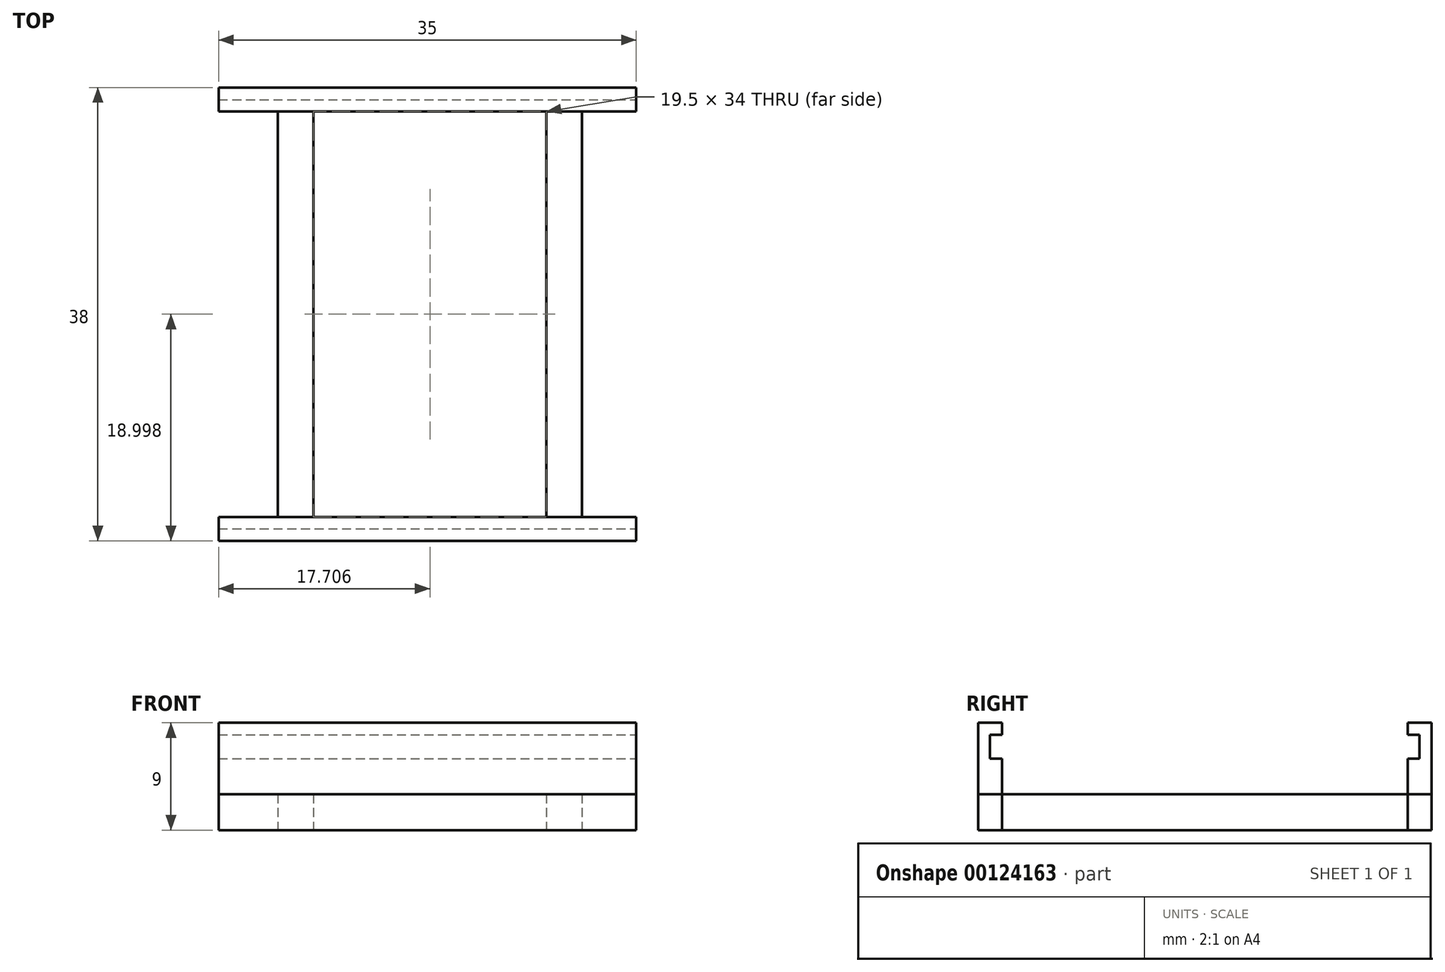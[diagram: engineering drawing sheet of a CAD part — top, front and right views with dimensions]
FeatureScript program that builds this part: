
annotation { "Feature Type Name" : "Feature", "Feature Type Description" : "" }
export const myFeature = defineFeature(function(context is Context, id is Id, definition is map)
    precondition{}
    {
        {
            var Q0;
            Q0=qCreatedBy(makeId("Top.planeOp"),FACE);
            var sketch = newSketch(context, id + "F0", { "sketchPlane" : qUnion([Q0])});
            skLineSegment(sketch, "E0.bottom", {"start": v(-16.7, 26) * mm, "end": v(18.3, 26) * mm});
            skLineSegment(sketch, "E0.top", {"start": v(-16.7, 24) * mm, "end": v(18.3, 24) * mm});
            skLineSegment(sketch, "E0.left", {"start": v(-16.7, 26) * mm, "end": v(-16.7, 24) * mm});
            skLineSegment(sketch, "E0.right", {"start": v(18.3, 26) * mm, "end": v(18.3, 24) * mm});
            skLineSegment(sketch, "E1.bottom", {"start": v(-16.7, -10) * mm, "end": v(18.3, -10) * mm});
            skLineSegment(sketch, "E1.top", {"start": v(-16.7, -12) * mm, "end": v(18.3, -12) * mm});
            skLineSegment(sketch, "E1.left", {"start": v(-16.7, -10) * mm, "end": v(-16.7, -12) * mm});
            skLineSegment(sketch, "E1.right", {"start": v(18.3, -10) * mm, "end": v(18.3, -12) * mm});
            skLineSegment(sketch, "E2.bottom", {"start": v(-11.74, 24) * mm, "end": v(-8.74, 24) * mm});
            skLineSegment(sketch, "E2.top", {"start": v(-11.74, -10) * mm, "end": v(-8.74, -10) * mm});
            skLineSegment(sketch, "E2.left", {"start": v(-11.74, 24) * mm, "end": v(-11.74, -10) * mm});
            skLineSegment(sketch, "E2.right", {"start": v(-8.74, 24) * mm, "end": v(-8.74, -10) * mm});
            skLineSegment(sketch, "E3.bottom", {"start": v(10.76, 24) * mm, "end": v(13.76, 24) * mm});
            skLineSegment(sketch, "E3.top", {"start": v(10.76, -10) * mm, "end": v(13.76, -10) * mm});
            skLineSegment(sketch, "E3.left", {"start": v(10.76, 24) * mm, "end": v(10.76, -10) * mm});
            skLineSegment(sketch, "E3.right", {"start": v(13.76, 24) * mm, "end": v(13.76, -10) * mm});
            skSolve(sketch);
        }
        {
            var Q0;
            Q0=makeQuery(id+"F0.imprint","IMPRINT",FACE,{"disambiguationData":[TD([[makeQuery(id+"F0.imprint","IMPRINT",EDGE,{"derivedFrom":sQuery(id+"F0.wireOp",EDGE,"E0.bottom")}),-1.0]])]});
            var Q1;
            Q1=makeQuery(id+"F0.imprint","IMPRINT",FACE,{"disambiguationData":[TD([[makeQuery(id+"F0.imprint","IMPRINT",EDGE,{"derivedFrom":sQuery(id+"F0.wireOp",EDGE,"E1.top")}),1.0]])]});
            extrude(context, id + "F1", {"entities" : qUnion([Q0, Q1]), "depth" : 9 * mm});
        }
        {
            var Q0;
            Q0 = qSketchRegion(id + "F0", true);
            extrude(context, id + "F2", {"entities" : qUnion([Q0]), "depth" : 3 * mm});
        }
        {
            var Q0;
            Q0=makeQuery(id+"F1.opExtrude","SWEPT_FACE",FACE,{"disambiguationData":[OSD([sQuery(id+"F0.wireOp",EDGE,"E1.right")])]});
            var sketch = newSketch(context, id + "F3", { "sketchPlane" : qUnion([Q0])});
            skLineSegment(sketch, "E4.bottom", {"start": v(-10, 8) * mm, "end": v(-11, 8) * mm});
            skLineSegment(sketch, "E4.top", {"start": v(-10, 6) * mm, "end": v(-11, 6) * mm});
            skLineSegment(sketch, "E4.left", {"start": v(-10, 8) * mm, "end": v(-10, 6) * mm});
            skLineSegment(sketch, "E4.right", {"start": v(-11, 8) * mm, "end": v(-11, 6) * mm});
            skSolve(sketch);
        }
        {
            var Q0;
            Q0 = qSketchRegion(id + "F3", true);
            extrude(context, id + "F4", {"entities" : qUnion([Q0]), "operationType" : NewBodyOperationType.REMOVE, "oppositeDirection" : true, "depth" : 35 * mm});
        }
        {
            var Q0;
            Q0=makeQuery(id+"F1.opExtrude","SWEPT_FACE",FACE,{"disambiguationData":[OSD([sQuery(id+"F0.wireOp",EDGE,"E0.right")])]});
            var sketch = newSketch(context, id + "F5", { "sketchPlane" : qUnion([Q0])});
            skLineSegment(sketch, "E5.bottom", {"start": v(24, 8) * mm, "end": v(25, 8) * mm});
            skLineSegment(sketch, "E5.top", {"start": v(24, 6) * mm, "end": v(25, 6) * mm});
            skLineSegment(sketch, "E5.left", {"start": v(24, 8) * mm, "end": v(24, 6) * mm});
            skLineSegment(sketch, "E5.right", {"start": v(25, 8) * mm, "end": v(25, 6) * mm});
            skSolve(sketch);
        }
        {
            var Q0;
            Q0=makeQuery(id+"F5.imprint","IMPRINT",FACE,{"disambiguationData":[TD([[makeQuery(id+"F5.imprint","IMPRINT",EDGE,{"derivedFrom":sQuery(id+"F5.wireOp",EDGE,"E5.bottom")}),-1.0]])]});
            extrude(context, id + "F6", {"entities" : qUnion([Q0]), "operationType" : NewBodyOperationType.REMOVE, "oppositeDirection" : true, "depth" : 35 * mm});
        }
    });
